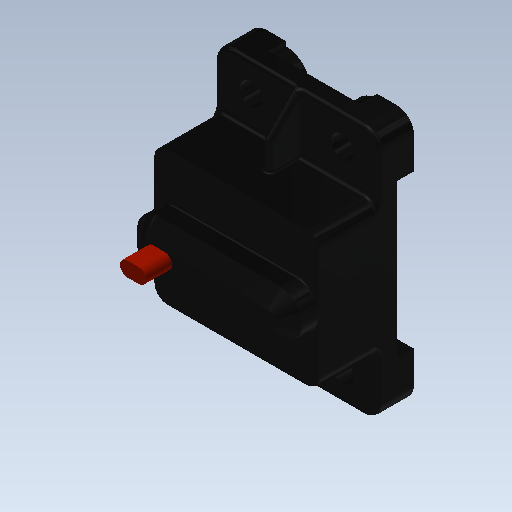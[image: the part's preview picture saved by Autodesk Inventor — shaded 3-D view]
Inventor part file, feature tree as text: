
AUTODESK INVENTOR PART (.ipt)
format: ipt  version: 2020 (Build 240168000, 168)  size: 387,072 bytes
history: native  units: mm (DEFAULTED — no unit token found)
features: fillet x7, sketch x7, extrude x6, mirror x3, chamfer x2, hole x1
ambient origin geometry x8: Origin, YZ Plane, XZ Plane, XY Plane, X Axis, Y Axis, Z Axis, Center Point
bodies: Solid1 (feature_tree)
feature tree (26):
  extrude  "Extrusion1"  Depth=73.406mm
  fillet  "Fillet1"  Radius=24.13mm
  extrude  "Extrusion2"  Depth=5.08mm TaperAngle=0.0deg
  fillet  "Fillet2"  Radius=5.08mm
  hole  "Hole1"  [1 undecoded]
  extrude  "Extrusion3"  Depth=10.795mm
  mirror  "Mirror3"
  mirror  "Mirror4"
  extrude  "Extrusion4"  Depth=14.224mm
  fillet  "Fillet3"  Radius=14.224mm
  chamfer  "Chamfer1"  Distance=5.08mm
  extrude  "Button"  Depth=0.635mm TaperAngle=0.0deg
  fillet  "Fillet4"  Radius=6.477mm
  fillet  "Fillet7"  Radius=3.81mm
  extrude  "Extrusion6"  Depth=0.635mm
  chamfer  "Chamfer2"  Distance=7.62mm
  fillet  "Fillet5"  Radius=2.159mm
  mirror  "Mirror5"
  fillet  "Fillet6"  Radius=7.62mm
  sketch  "Sketch1"  dims[d0=48.26mm d1=73.406mm d2=24.13mm]
  sketch  "Sketch2"  dims[d3=36.703mm d4=5.08mm d5=0.0mm d6=5.08mm]
  sketch  "Sketch3"  dims[d7=39.37mm d8=17.526mm d9=0.0mm]
  sketch  "Sketch5"  dims[d10=3.81mm d11=10.795mm]
  sketch  "Sketch6"  dims[d12=8.382mm]
  sketch  "Sketch7"  dims[d13=6.604mm d14=12.7mm d15=9.525mm d16=6.35mm d17=14.3117mm d18=19.05mm d19=20.594885mm d20=14.224mm d21=14.224mm d23=5.08mm d24=0.0mm]
  sketch  "Sketch8"  dims[d25=12.954mm d26=8.89mm d27=0.0mm d28=6.477mm d29=3.81mm d30=3.81mm d31=4.318mm d32=7.62mm d33=2.159mm d34=7.62mm d35=0.0mm d36=2.159mm d37=2.54mm d38=1.27mm d39=8.89mm d40=0.0mm d41=8.89mm d42=8.89mm d43=1.27mm d44=1.27mm d45=0.635mm d46=1.27mm d47=45.0deg d48=45.0deg]
note: 1 required parameter value undecoded (feature->parameter linkage not recoverable at this tier; creation-order binding heuristic only, values carry confidence <= 0.55)
